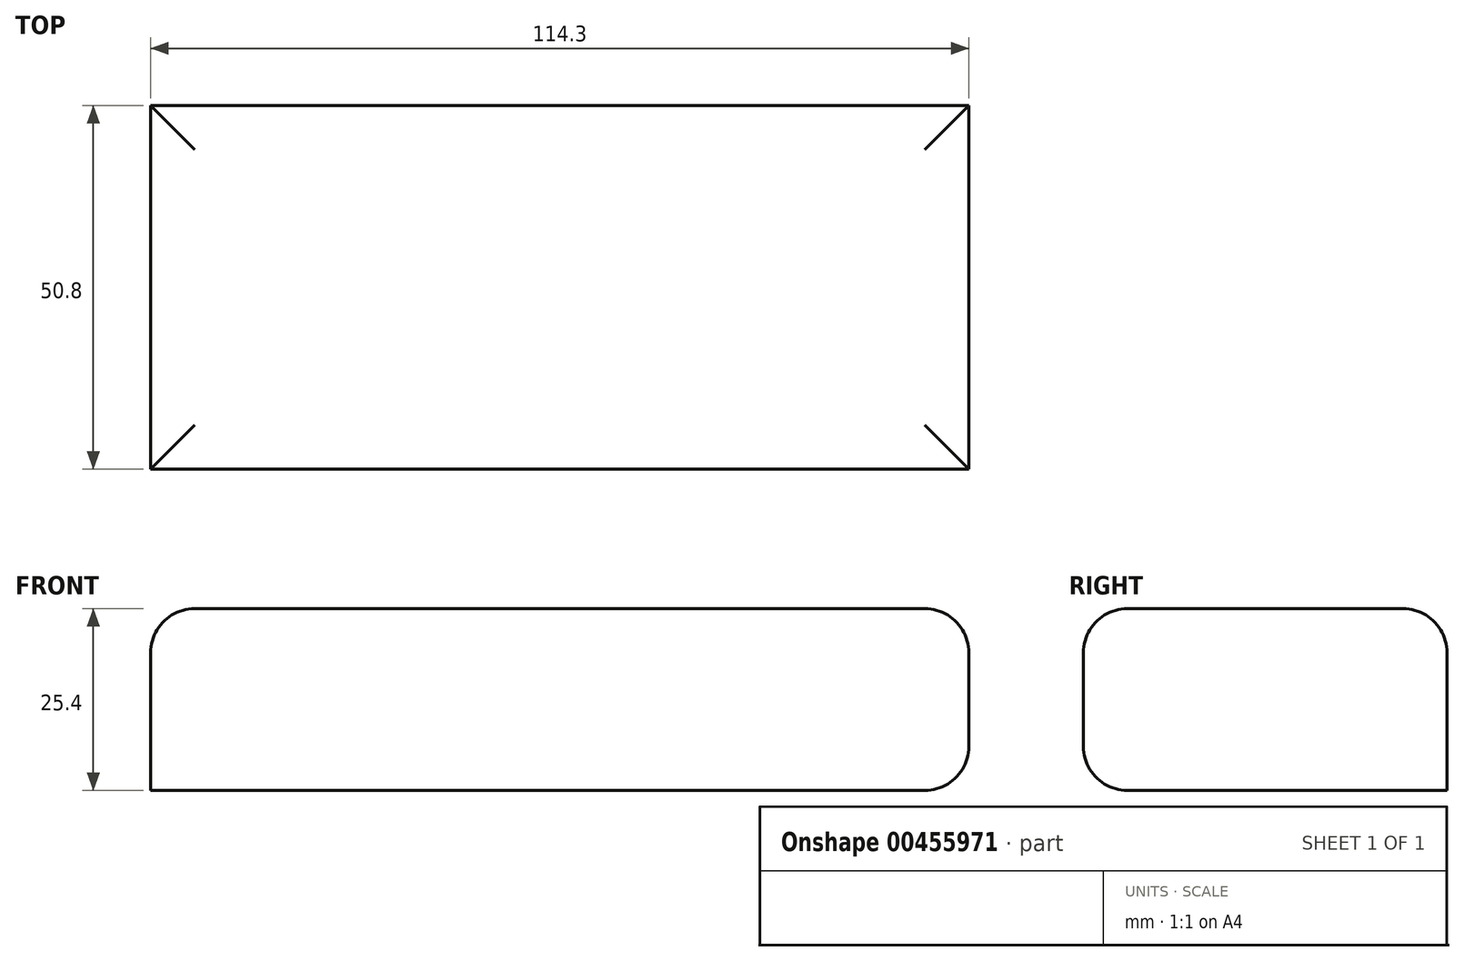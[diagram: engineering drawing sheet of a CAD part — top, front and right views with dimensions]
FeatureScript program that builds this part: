
annotation { "Feature Type Name" : "Feature", "Feature Type Description" : "" }
export const myFeature = defineFeature(function(context is Context, id is Id, definition is map)
    precondition{}
    {
        {
            var Q0;
            Q0=qCreatedBy(makeId("Top.planeOp"),FACE);
            var sketch = newSketch(context, id + "F0", { "sketchPlane" : qUnion([Q0])});
            skLineSegment(sketch, "E0.bottom", {"start": v(57.15, 25.4) * mm, "end": v(-57.15, 25.4) * mm});
            skLineSegment(sketch, "E0.top", {"start": v(57.15, -25.4) * mm, "end": v(-57.15, -25.4) * mm});
            skLineSegment(sketch, "E0.left", {"start": v(57.15, 25.4) * mm, "end": v(57.15, -25.4) * mm});
            skLineSegment(sketch, "E0.right", {"start": v(-57.15, 25.4) * mm, "end": v(-57.15, -25.4) * mm});
            skPoint(sketch, "E0.middle", {"position": v(0, 0) * mm});
            skSolve(sketch);
        }
        {
            var Q0;
            Q0 = qSketchRegion(id + "F0", true);
            extrude(context, id + "F1", {"entities" : qUnion([Q0]), "depth" : 25.4 * mm});
        }
        {
            var Q0;
            Q0=makeQuery(id+"F1.opExtrude","CAP_EDGE",EDGE,{"disambiguationData":[OSD([sQuery(id+"F0.wireOp",EDGE,"E0.left")])],"isStart":true});
            var Q1;
            Q1=makeQuery(id+"F1.opExtrude","CAP_EDGE",EDGE,{"disambiguationData":[OSD([sQuery(id+"F0.wireOp",EDGE,"E0.right")])],"isStart":false});
            var Q2;
            Q2=makeQuery(id+"F1.opExtrude","CAP_EDGE",EDGE,{"disambiguationData":[OSD([sQuery(id+"F0.wireOp",EDGE,"E0.top")])],"isStart":false});
            var Q3;
            Q3=makeQuery(id+"F1.opExtrude","CAP_EDGE",EDGE,{"disambiguationData":[OSD([sQuery(id+"F0.wireOp",EDGE,"E0.bottom")])],"isStart":false});
            var Q4;
            Q4=makeQuery(id+"F1.opExtrude","CAP_EDGE",EDGE,{"disambiguationData":[OSD([sQuery(id+"F0.wireOp",EDGE,"E0.left")])],"isStart":false});
            var Q5;
            Q5=makeQuery(id+"F1.opExtrude","CAP_EDGE",EDGE,{"disambiguationData":[OSD([sQuery(id+"F0.wireOp",EDGE,"E0.top")])],"isStart":true});
            fillet(context, id + "F2", {"entities" : qUnion([Q0, Q1, Q2, Q3, Q4, Q5]), "radius" : 6.13 * mm, "tangentPropagation" : true, "allowEdgeOverflow" : false});
        }
    });
